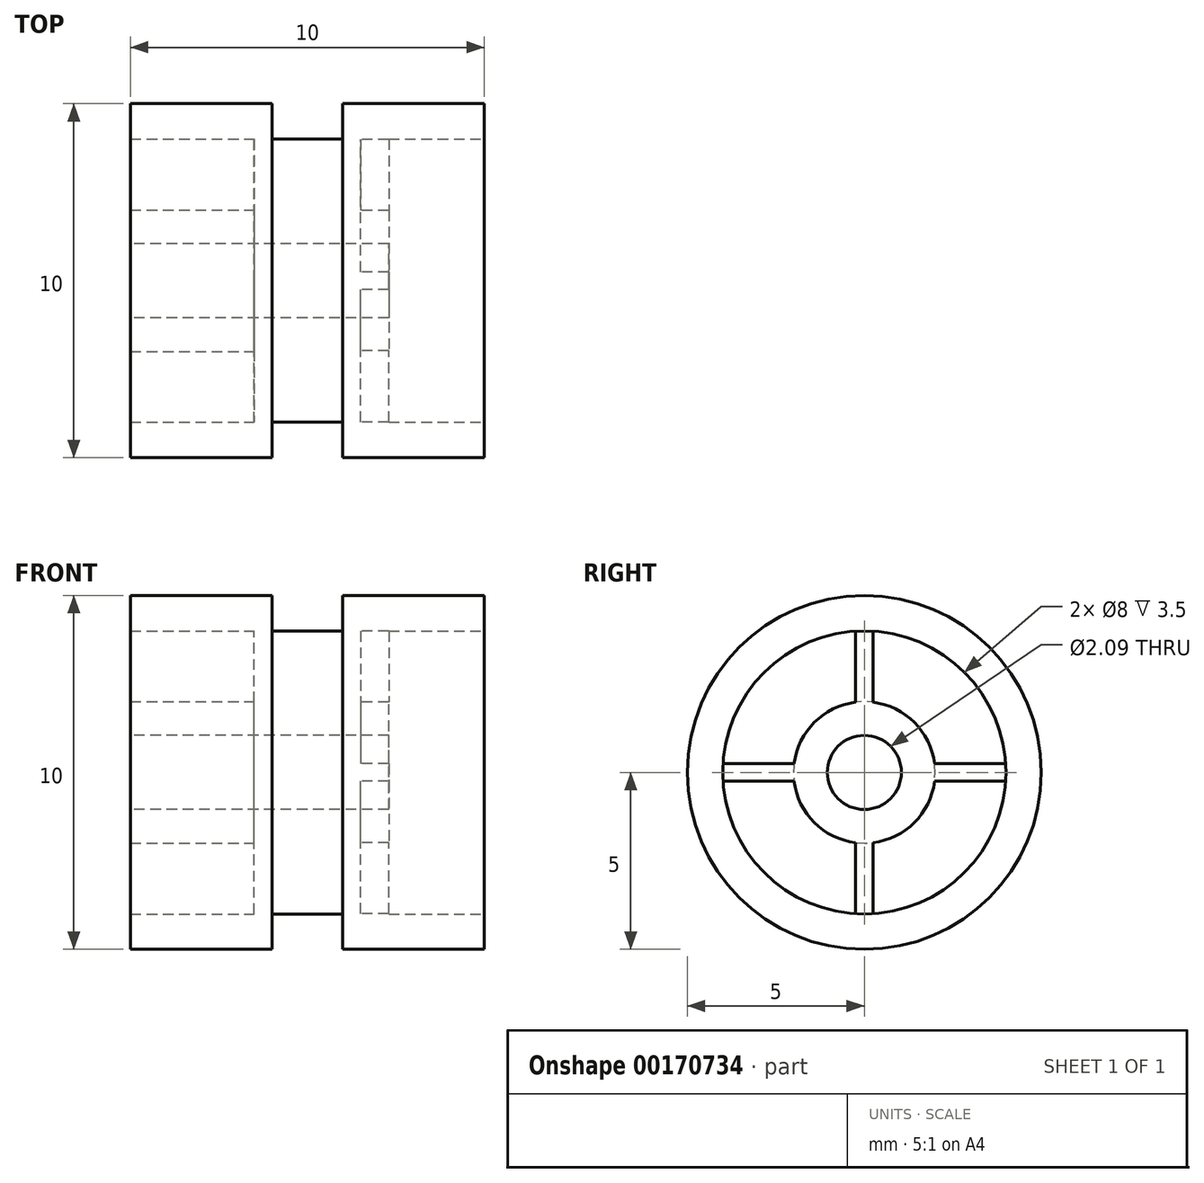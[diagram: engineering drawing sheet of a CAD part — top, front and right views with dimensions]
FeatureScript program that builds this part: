
annotation { "Feature Type Name" : "Feature", "Feature Type Description" : "" }
export const myFeature = defineFeature(function(context is Context, id is Id, definition is map)
    precondition{}
    {
        {
            var Q0;
            Q0=qCreatedBy(makeId("Front.planeOp"),FACE);
            var sketch = newSketch(context, id + "F0", { "sketchPlane" : qUnion([Q0])});
            skLineSegment(sketch, "E0", {"start": v(0, 0) * mm, "end": v(-127, 0) * mm});
            skLineSegment(sketch, "E1", {"start": v(-127, 0) * mm, "end": v(-127, 50.8) * mm});
            skLineSegment(sketch, "E2", {"start": v(-38.1, 76.2) * mm, "end": v(-38.1, 101.6) * mm});
            skLineSegment(sketch, "E3", {"start": v(-38.1, 101.6) * mm, "end": v(-127, 101.6) * mm});
            skLineSegment(sketch, "E4", {"start": v(-127, 101.6) * mm, "end": v(-127, 127) * mm});
            skLineSegment(sketch, "E5", {"start": v(-127, 127) * mm, "end": v(-25.4, 127) * mm});
            skLineSegment(sketch, "E6", {"start": v(-25.4, 127) * mm, "end": v(-25.4, 101.6) * mm});
            skLineSegment(sketch, "E7", {"start": v(-25.4, 101.6) * mm, "end": v(0, 101.6) * mm});
            skLineSegment(sketch, "E8.MirrorCS", {"start": v(-38.1, 76.2) * mm, "end": v(-38.1, 50.8) * mm});
            skLineSegment(sketch, "E9.MirrorCS", {"start": v(-38.1, 50.8) * mm, "end": v(-127, 50.8) * mm});
            skLineSegment(sketch, "E10.MirrorCS", {"start": v(-127, 50.8) * mm, "end": v(-127, 25.4) * mm});
            skLineSegment(sketch, "E11.MirrorCS", {"start": v(38.1, 76.2) * mm, "end": v(38.1, 50.8) * mm});
            skLineSegment(sketch, "E12.MirrorCS", {"start": v(38.1, 76.2) * mm, "end": v(38.1, 101.6) * mm});
            skLineSegment(sketch, "E13.MirrorCS", {"start": v(38.1, 101.6) * mm, "end": v(127, 101.6) * mm});
            skLineSegment(sketch, "E14.MirrorCS", {"start": v(127, 101.6) * mm, "end": v(127, 127) * mm});
            skLineSegment(sketch, "E15.MirrorCS", {"start": v(127, 127) * mm, "end": v(25.4, 127) * mm});
            skLineSegment(sketch, "E16.MirrorCS", {"start": v(25.4, 127) * mm, "end": v(25.4, 101.6) * mm});
            skLineSegment(sketch, "E17.MirrorCS", {"start": v(25.4, 101.6) * mm, "end": v(0, 101.6) * mm});
            skPoint(sketch, "E18.MirrorCS.end.orphan", {"position": v(38.1, 76.2) * mm});
            skPoint(sketch, "E18.MirrorCS.start.orphan", {"position": v(127, 76.2) * mm});
            skLineSegment(sketch, "E19", {"start": v(38.1, 50.8) * mm, "end": v(38.1, 0) * mm});
            skLineSegment(sketch, "E20", {"start": v(38.1, 0) * mm, "end": v(0, 0) * mm});
            skPoint(sketch, "E21.orphan", {"position": v(-127, 76.2) * mm});
            skSolve(sketch);
        }
        {
            var Q0;
            Q0=makeQuery(id+"F0.imprint","IMPRINT",FACE,{"disambiguationData":[TD([[makeQuery(id+"F0.imprint","IMPRINT",EDGE,{"derivedFrom":sQuery(id+"F0.wireOp",EDGE,"E0")}),-1.0]])]});
            var Q1;
            Q1=sQuery(id+"F0.wireOp",EDGE,"E0");
            revolve(context, id + "F1", {"entities" : qUnion([Q0]), "axis" : qUnion([Q1]), "revolveType" : RevolveType.FULL});
        }
        {
            var Q0;
            Q0=makeQuery(id+"F1.opRevolve","SWEPT_FACE",FACE,{"disambiguationData":[OSD([sQuery(id+"F0.wireOp",EDGE,"E11.MirrorCS"),sQuery(id+"F0.wireOp",EDGE,"E12.MirrorCS"),sQuery(id+"F0.wireOp",EDGE,"E19")])]});
            var sketch = newSketch(context, id + "F2", { "sketchPlane" : qUnion([Q0])});
            skCircle(sketch, "E22", {"center": v(0, 0) * mm, "radius": 50.8 * mm});
            skArc(sketch, "E23.0", {"start": v(6.35, 101.4) * mm, "mid": v(0, 101.6) * mm, "end": v(-6.35, 101.4) * mm});
            skLineSegment(sketch, "E24.0", {"start": v(-6.35, 101.6) * mm, "end": v(-6.35, 50.4) * mm});
            skLineSegment(sketch, "E25.0", {"start": v(6.35, 101.6) * mm, "end": v(6.35, 50.4) * mm});
            skLineSegment(sketch, "E26.1.0", {"start": v(-101.74, -6.35) * mm, "end": v(-50.4, -6.35) * mm});
            skLineSegment(sketch, "E26.1.1", {"start": v(-101.6, 6.35) * mm, "end": v(-50.4, 6.35) * mm});
            skLineSegment(sketch, "E26.2.0", {"start": v(6.35, -101.6) * mm, "end": v(6.35, -50.4) * mm});
            skLineSegment(sketch, "E26.2.1", {"start": v(-6.35, -101.6) * mm, "end": v(-6.35, -50.4) * mm});
            skLineSegment(sketch, "E26.3.0", {"start": v(101.6, 6.35) * mm, "end": v(50.4, 6.35) * mm});
            skLineSegment(sketch, "E26.3.1", {"start": v(101.6, -6.35) * mm, "end": v(50.4, -6.35) * mm});
            skPoint(sketch, "E27.orphan", {"position": v(-50.8, 6.35) * mm});
            skPoint(sketch, "E28.orphan", {"position": v(-50.8, -6.35) * mm});
            skPoint(sketch, "E29.orphan", {"position": v(-6.35, 50.8) * mm});
            skPoint(sketch, "E30.orphan", {"position": v(6.35, 50.8) * mm});
            skPoint(sketch, "E31.orphan", {"position": v(50.8, 6.35) * mm});
            skPoint(sketch, "E32.orphan", {"position": v(50.8, -6.35) * mm});
            skPoint(sketch, "E33.orphan", {"position": v(6.35, -50.8) * mm});
            skPoint(sketch, "E34.orphan", {"position": v(-6.35, -50.8) * mm});
            skPoint(sketch, "E35.orphan", {"position": v(-6.35, -101.6) * mm});
            skPoint(sketch, "E36.orphan", {"position": v(6.35, -101.6) * mm});
            skPoint(sketch, "E37.orphan", {"position": v(101.6, -6.35) * mm});
            skPoint(sketch, "E38.orphan", {"position": v(101.6, 6.35) * mm});
            skPoint(sketch, "E39.orphan", {"position": v(-101.6, -6.35) * mm});
            skPoint(sketch, "E40.orphan", {"position": v(-101.6, 6.35) * mm});
            skPoint(sketch, "E41.orphan", {"position": v(-6.35, 101.6) * mm});
            skPoint(sketch, "E42.orphan", {"position": v(6.35, 101.6) * mm});
            skArc(sketch, "E43.trimOffspring", {"start": v(-101.4, 6.35) * mm, "mid": v(-101.6, 0) * mm, "end": v(-101.4, -6.35) * mm});
            skArc(sketch, "E44.trimOffspring", {"start": v(-6.35, -101.4) * mm, "mid": v(0, -101.6) * mm, "end": v(6.35, -101.4) * mm});
            skArc(sketch, "E45.trimOffspring", {"start": v(101.4, -6.35) * mm, "mid": v(101.6, 0) * mm, "end": v(101.4, 6.35) * mm});
            skSolve(sketch);
        }
        {
            var Q0;
            Q0 = qSketchRegion(id + "F2", true);
            extrude(context, id + "F3", {"entities" : qUnion([Q0]), "operationType" : NewBodyOperationType.ADD, "depth" : (2.54 * 8) * mm});
        }
        {
            var Q0;
            Q0=makeQuery(id+"F1.opRevolve","SWEPT_FACE",FACE,{"disambiguationData":[OSD([sQuery(id+"F0.wireOp",EDGE,"E1"),sQuery(id+"F0.wireOp",EDGE,"E10.MirrorCS")])]});
            var sketch = newSketch(context, id + "F4", { "sketchPlane" : qUnion([Q0])});
            skCircle(sketch, "E46", {"center": v(0, 0) * mm, "radius": 26.6 * mm});
            skSolve(sketch);
        }
        {
            var Q0;
            Q0=makeQuery(id+"F4.imprint","IMPRINT",FACE,{"disambiguationData":[TD([[makeQuery(id+"F4.imprint","IMPRINT",EDGE,{"derivedFrom":sQuery(id+"F4.wireOp",EDGE,"E46")}),1.0]])]});
            extrude(context, id + "F5", {"entities" : qUnion([Q0]), "operationType" : NewBodyOperationType.REMOVE, "endBound" : BoundingType.THROUGH_ALL, "oppositeDirection" : true, "depth" : 25 * mm});
        }
        {
            var Q0;
            Q0=makeQuery(id+"F1.opRevolve","SWEPT_BODY",BODY,{"disambiguationData":[OSD([sQuery(id+"F0.wireOp",EDGE,"E0"),sQuery(id+"F0.wireOp",EDGE,"E1"),sQuery(id+"F0.wireOp",EDGE,"E2"),sQuery(id+"F0.wireOp",EDGE,"E3"),sQuery(id+"F0.wireOp",EDGE,"E4"),sQuery(id+"F0.wireOp",EDGE,"E5"),sQuery(id+"F0.wireOp",EDGE,"E6"),sQuery(id+"F0.wireOp",EDGE,"E7"),sQuery(id+"F0.wireOp",EDGE,"E10.MirrorCS"),sQuery(id+"F0.wireOp",EDGE,"E9.MirrorCS"),sQuery(id+"F0.wireOp",EDGE,"E8.MirrorCS"),sQuery(id+"F0.wireOp",EDGE,"E11.MirrorCS"),sQuery(id+"F0.wireOp",EDGE,"E12.MirrorCS"),sQuery(id+"F0.wireOp",EDGE,"E13.MirrorCS"),sQuery(id+"F0.wireOp",EDGE,"E14.MirrorCS"),sQuery(id+"F0.wireOp",EDGE,"E15.MirrorCS"),sQuery(id+"F0.wireOp",EDGE,"E16.MirrorCS"),sQuery(id+"F0.wireOp",EDGE,"E17.MirrorCS"),sQuery(id+"F0.wireOp",EDGE,"E19"),sQuery(id+"F0.wireOp",EDGE,"E20")])]});
            var Q1;
            Q1=qCreatedBy(makeId("Origin.pointOp"),VERTEX);
            transform(context, id + "F6", {"entities" : qUnion([Q0]), "transformType" : TransformType.SCALE_UNIFORMLY, "scale" : 1 / 25.4, "scalePoint" : qUnion([Q1]), "makeCopy" : false});
        }
    });
